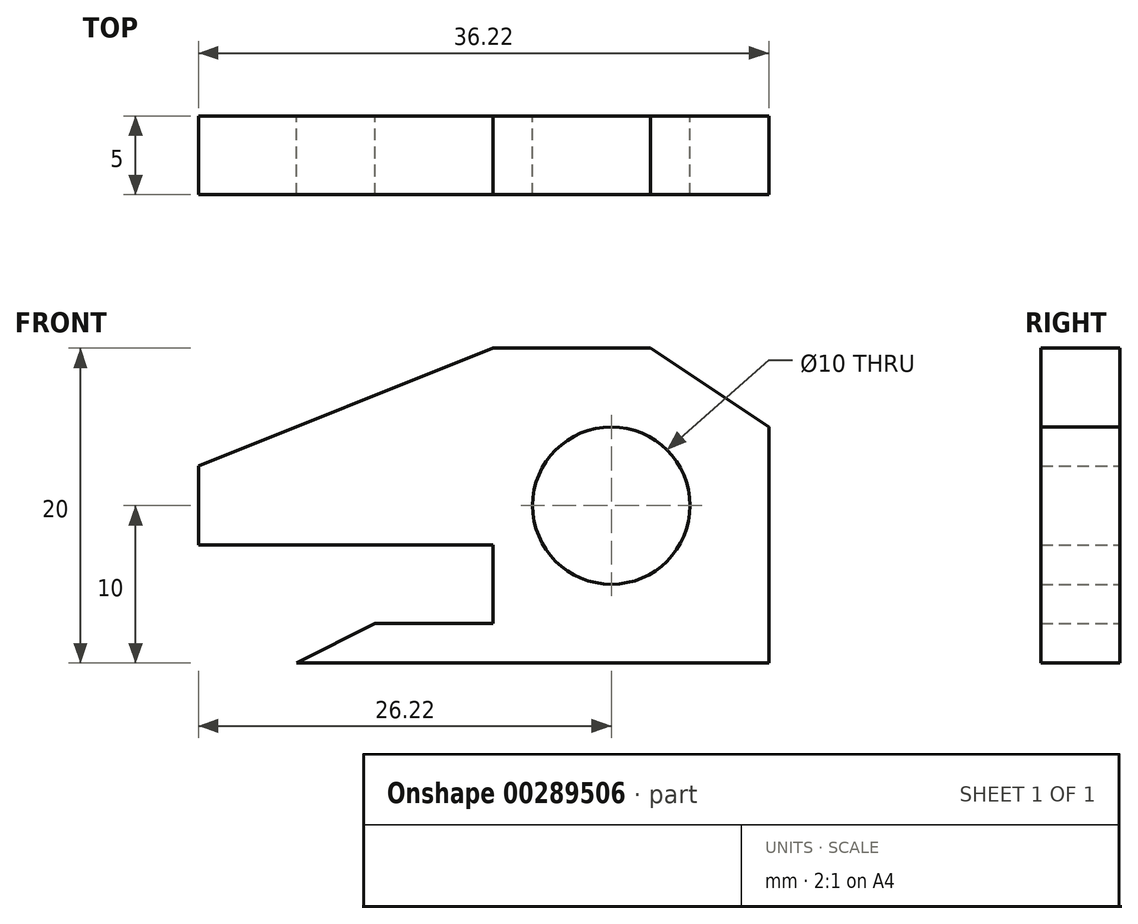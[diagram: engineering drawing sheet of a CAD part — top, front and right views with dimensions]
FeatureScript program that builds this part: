
annotation { "Feature Type Name" : "Feature", "Feature Type Description" : "" }
export const myFeature = defineFeature(function(context is Context, id is Id, definition is map)
    precondition{}
    {
        {
            var Q0;
            Q0=qCreatedBy(makeId("Front.planeOp"),FACE);
            var sketch = newSketch(context, id + "F0", { "sketchPlane" : qUnion([Q0])});
            skLineSegment(sketch, "E0", {"start": v(0, 0) * mm, "end": v(-30, 0) * mm});
            skLineSegment(sketch, "E1", {"start": v(-30, 0) * mm, "end": v(-25, 2.5) * mm});
            skLineSegment(sketch, "E2", {"start": v(-25, 2.5) * mm, "end": v(-17.5, 2.5) * mm});
            skLineSegment(sketch, "E3", {"start": v(-17.5, 2.5) * mm, "end": v(-17.5, 7.5) * mm});
            skLineSegment(sketch, "E4", {"start": v(-17.5, 7.5) * mm, "end": v(-36.22, 7.5) * mm});
            skLineSegment(sketch, "E5", {"start": v(-36.22, 7.5) * mm, "end": v(-36.22, 12.5) * mm});
            skLineSegment(sketch, "E6", {"start": v(-36.22, 12.5) * mm, "end": v(-17.5, 20) * mm});
            skLineSegment(sketch, "E7", {"start": v(-17.5, 20) * mm, "end": v(-7.5, 20) * mm});
            skLineSegment(sketch, "E8", {"start": v(-7.5, 20) * mm, "end": v(0, 15) * mm});
            skLineSegment(sketch, "E9", {"start": v(0, 15) * mm, "end": v(0, 0) * mm});
            skCircle(sketch, "E10", {"center": v(-10, 10) * mm, "radius": 5 * mm});
            skSolve(sketch);
        }
        {
            var Q0;
            Q0 = qSketchRegion(id + "F0", true);
            extrude(context, id + "F1", {"entities" : qUnion([Q0]), "depth" : 5 * mm});
        }
    });
